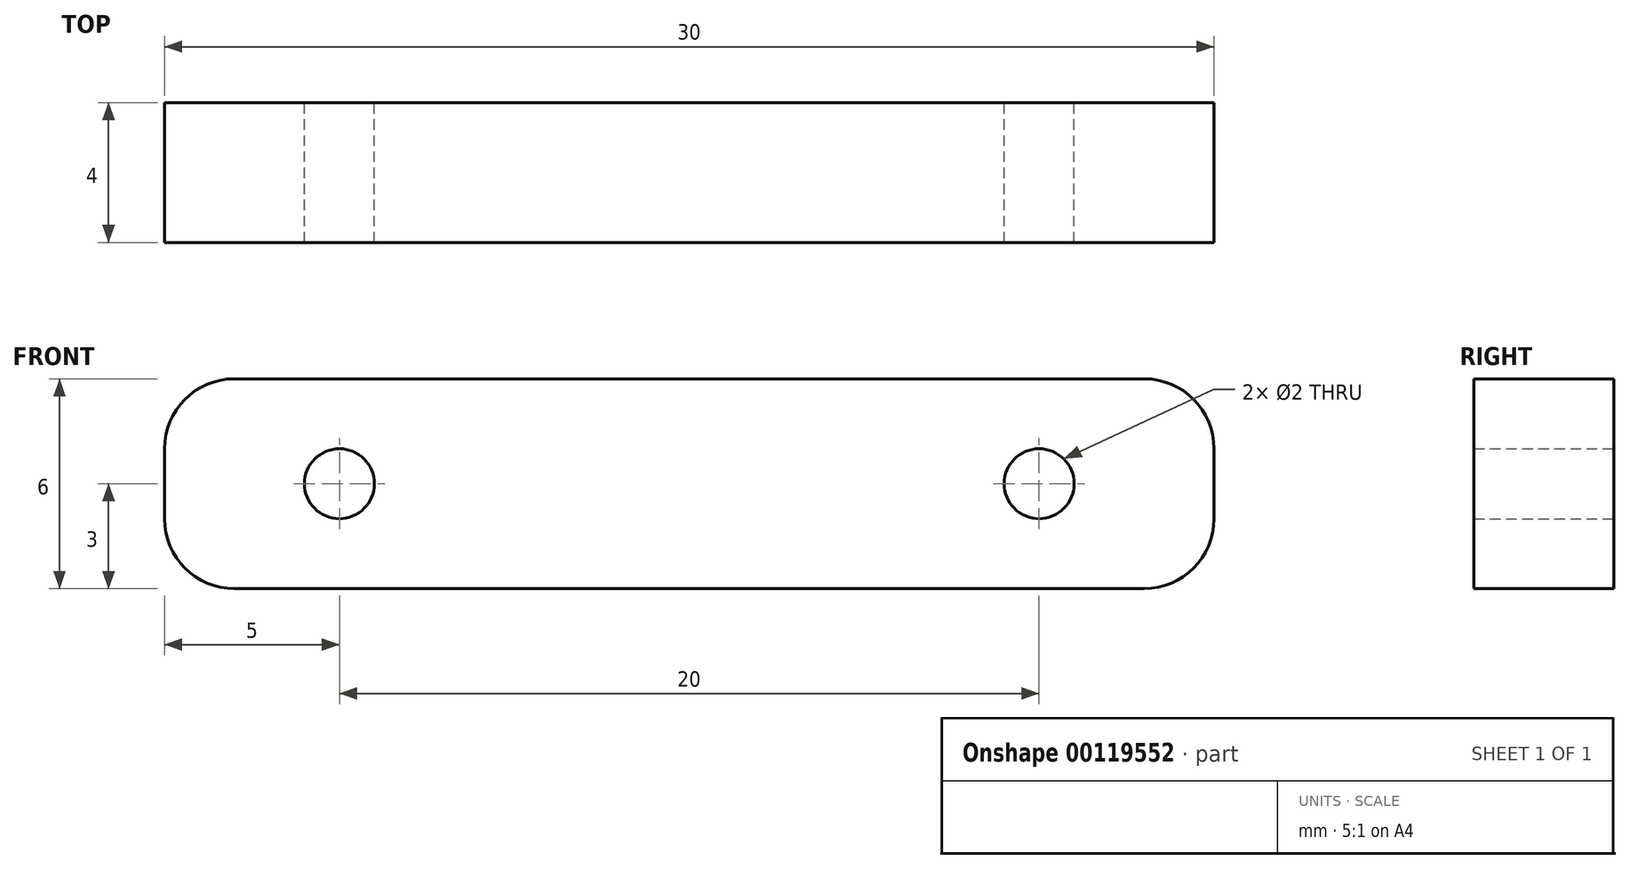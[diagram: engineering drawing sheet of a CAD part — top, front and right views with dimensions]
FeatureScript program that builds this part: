
annotation { "Feature Type Name" : "Feature", "Feature Type Description" : "" }
export const myFeature = defineFeature(function(context is Context, id is Id, definition is map)
    precondition{}
    {
        {
            var Q0;
            Q0=qCreatedBy(makeId("Front.planeOp"),FACE);
            var sketch = newSketch(context, id + "F0", { "sketchPlane" : qUnion([Q0])});
            skLineSegment(sketch, "E0.bottom", {"start": v(-13, 3) * mm, "end": v(13, 3) * mm});
            skLineSegment(sketch, "E0.top", {"start": v(-13, -3) * mm, "end": v(13, -3) * mm});
            skLineSegment(sketch, "E0.left", {"start": v(-15, 1) * mm, "end": v(-15, -1) * mm});
            skLineSegment(sketch, "E0.right", {"start": v(15, 1) * mm, "end": v(15, -1) * mm});
            skPoint(sketch, "E0.middle", {"position": v(0, 0) * mm});
            skPoint(sketch, "E1.visualSharp", {"position": v(-15, 3) * mm});
            skArc(sketch, "E1.filletArc", {"start": v(-13, 3) * mm, "mid": v(-14.41, 2.41) * mm, "end": v(-15, 1) * mm});
            skPoint(sketch, "E2.visualSharp", {"position": v(-15, -3) * mm});
            skArc(sketch, "E2.filletArc", {"start": v(-15, -1) * mm, "mid": v(-14.41, -2.41) * mm, "end": v(-13, -3) * mm});
            skPoint(sketch, "E3.visualSharp", {"position": v(15, -3) * mm});
            skArc(sketch, "E3.filletArc", {"start": v(13, -3) * mm, "mid": v(14.41, -2.41) * mm, "end": v(15, -1) * mm});
            skPoint(sketch, "E4.visualSharp", {"position": v(15, 3) * mm});
            skArc(sketch, "E4.filletArc", {"start": v(15, 1) * mm, "mid": v(14.41, 2.41) * mm, "end": v(13, 3) * mm});
            skCircle(sketch, "E5", {"center": v(-10, 0) * mm, "radius": 1 * mm});
            skCircle(sketch, "E6", {"center": v(10, 0) * mm, "radius": 1 * mm});
            skSolve(sketch);
        }
        {
            var Q0;
            Q0=makeQuery(id+"F0.imprint","IMPRINT",FACE,{"disambiguationData":[TD([[makeQuery(id+"F0.imprint","IMPRINT",EDGE,{"derivedFrom":sQuery(id+"F0.wireOp",EDGE,"E0.bottom")}),-1.0]])]});
            extrude(context, id + "F1", {"entities" : qUnion([Q0]), "depth" : 4 * mm});
        }
    });
